# Revit family: Electrical_Equipment-Floor_Box-Hubbell_Wiring-CFBS1R4PFB
name_source: partatom
category: Electrical Fixtures
revit_build: Autodesk Revit 2015 (Build: 20140606_1530(x64)
units: mm (PartAtom-declared; Revit-internal decimal feet)

## types (1)
- CFBS1R4PFB
    Assembly Code = D5020115
    Conduit Connector_1 Description = 1.5in. 1.25in. or 1in. Reducers/Plugs
    Conduit Connector_2 Description = 1.5in. 1.25 in. or 1in. Reducers/Plugs
    Conduit Connector_3 Description = 1in. 0.75in. or 0.5in. Reducers/Plugs
    Conduit Connector_4 Description = 1in. 0.75in. or 0.5in. Reducers/Plugs
    Cover Material = Metal-Hubbell-Aluminum
    Default Elevation = 48 "
    Description = Plastic Recessed Floor Box, 4in Round Cover
    Manufacturer = Hubbell Wiring Device
    Manufacturer Fax = 203-882-4852
    Model = CFBS1R4PFB
    Product Documentation Link = http://www.hubbell-wiring.com
    Product Material = Non_Metallic-Hubbell-Gray
    Product Page URL = http://www.hubbell-wiring.com
    Product data url = https://bimobject.com
    URL = http://www.hubbell-wiring.com

## geometry (parser evidence)
native form markers: Blend x34, Sweep x2
no freeform markers — native parametric forms only
